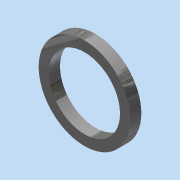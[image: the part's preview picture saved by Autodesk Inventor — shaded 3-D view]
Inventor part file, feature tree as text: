
AUTODESK INVENTOR PART (.ipt)
format: ipt  version: 2015 (Build 190159000, 159)  size: 83,456 bytes
history: native  units: in
note: dims shown in document units (in); Inventor stores cm internally (conversion verified against a paired STEP export)
features: extrude x1, sketch x1
ambient origin geometry x8: Origin, YZ Plane, XZ Plane, XY Plane, X Axis, Y Axis, Z Axis, Center Point
bodies: Solid1 (feature_tree)
feature tree (2):
  extrude  "Extrusion1"  Depth=0.2756in
  sketch  "Sketch1"  dims[d0=1.7717in d1=2.2835in d2=0.2756in d3=0.0in]
